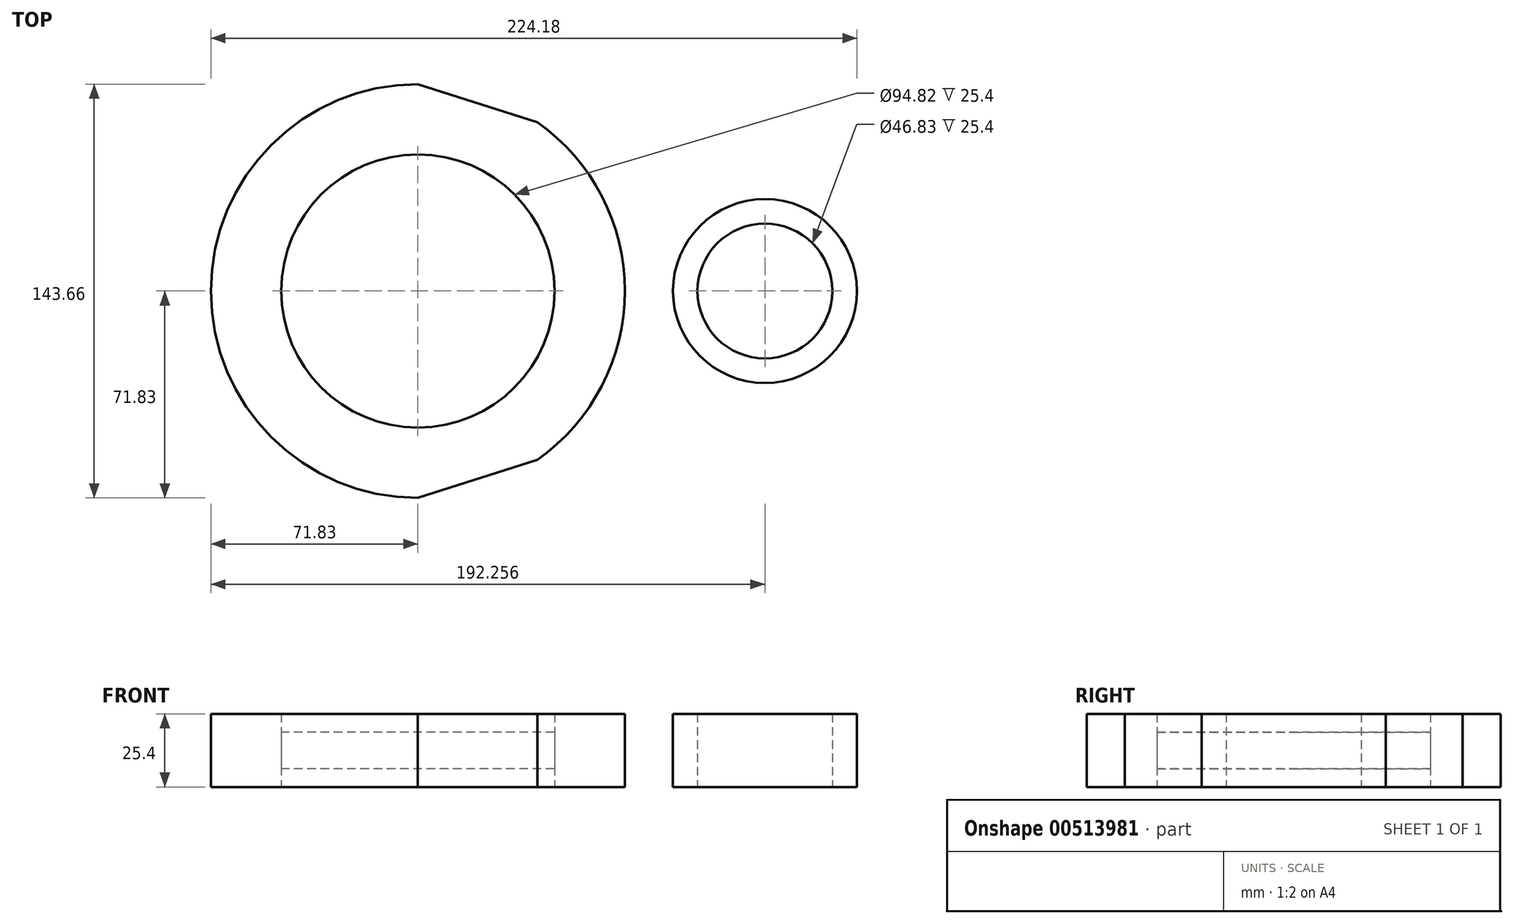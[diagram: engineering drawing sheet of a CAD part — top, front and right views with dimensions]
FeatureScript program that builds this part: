
annotation { "Feature Type Name" : "Feature", "Feature Type Description" : "" }
export const myFeature = defineFeature(function(context is Context, id is Id, definition is map)
    precondition{}
    {
        {
            var Q0;
            Q0=qCreatedBy(makeId("Top.planeOp"),FACE);
            var sketch = newSketch(context, id + "F0", { "sketchPlane" : qUnion([Q0])});
            skCircle(sketch, "E0", {"center": v(0, 0) * mm, "radius": 71.83 * mm});
            skCircle(sketch, "E1", {"center": v(0, 0) * mm, "radius": 47.41 * mm});
            skCircle(sketch, "E2", {"center": v(120.43, 0) * mm, "radius": 31.93 * mm});
            skCircle(sketch, "E3", {"center": v(120.43, 0) * mm, "radius": 23.41 * mm});
            skLineSegment(sketch, "E4", {"start": v(0, 71.83) * mm, "end": v(130.1, 30.42) * mm});
            skLineSegment(sketch, "E5", {"start": v(0, -71.83) * mm, "end": v(130.1, -30.42) * mm});
            skSolve(sketch);
        }
        {
            var Q0;
            Q0=makeQuery(id+"F0.imprint","IMPRINT",FACE,{"disambiguationData":[TD([[makeQuery(id+"F0.imprint","IMPRINT",EDGE,{"derivedFrom":sQuery(id+"F0.wireOp",EDGE,"E1")}),-1.0]])]});
            var Q1;
            Q1=makeQuery(id+"F0.imprint","IMPRINT",FACE,{"disambiguationData":[TD([[makeQuery(id+"F0.imprint","IMPRINT",EDGE,{"derivedFrom":sQuery(id+"F0.wireOp",EDGE,"E3")}),-1.0]])]});
            extrude(context, id + "F1", {"entities" : qUnion([Q0, Q1]), "endBound" : BoundingType.SYMMETRIC, "depth" : 25.4 * mm});
        }
        {
            var Q0;
            Q0=makeQuery(id+"F0.imprint","IMPRINT",FACE,{"disambiguationData":[TD([[makeQuery(id+"F0.imprint","IMPRINT",EDGE,{"derivedFrom":sQuery(id+"F0.wireOp",EDGE,"E1")}),1.0]])]});
            var Q1;
            {var subQ0=sQuery(id+"F0.wireOp",EDGE,"E4");var subQ1=sQuery(id+"F0.wireOp",EDGE,"E0");var subQ2=makeQuery(id+"F0.imprint","INTERSECT",VERTEX,{"disambiguationData":[OD(1.0)],"derivedFrom":[subQ1,subQ0]});Q1=makeQuery(id+"F0.imprint","IMPRINT",FACE,{"disambiguationData":[TD([[makeQuery(id+"F0.imprint","IMPRINT",EDGE,{"disambiguationData":[TD([[subQ2,1.0]])],"derivedFrom":subQ1}),-1.0]])]});}
            extrude(context, id + "F2", {"entities" : qUnion([Q0, Q1]), "endBound" : BoundingType.SYMMETRIC, "depth" : 12.7 * mm});
        }
    });
